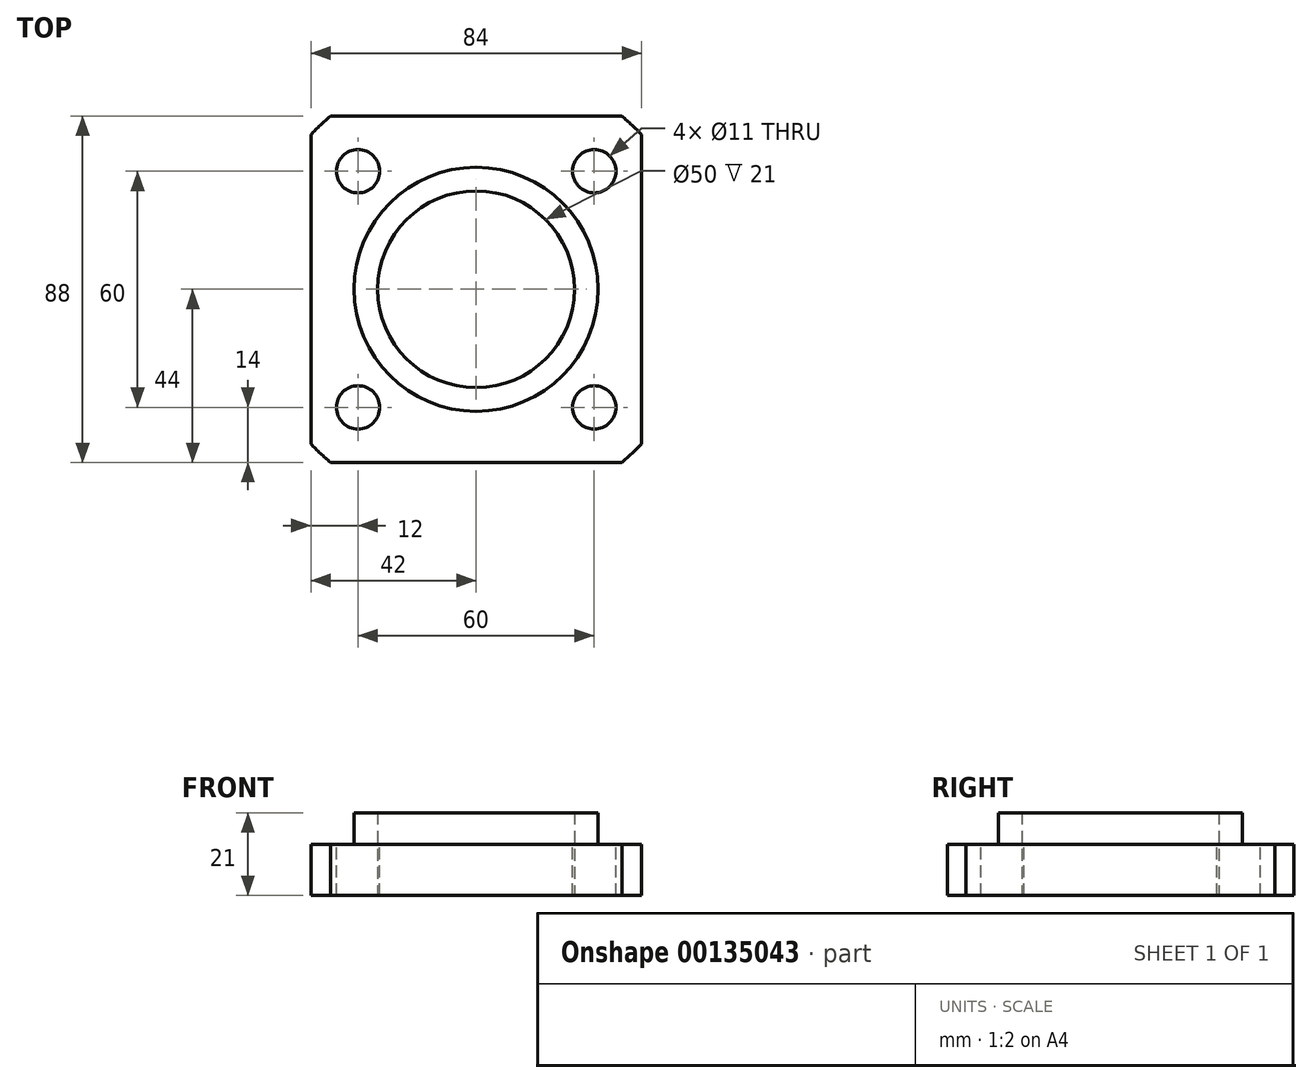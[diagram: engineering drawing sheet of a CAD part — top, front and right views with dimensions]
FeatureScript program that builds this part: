
annotation { "Feature Type Name" : "Feature", "Feature Type Description" : "" }
export const myFeature = defineFeature(function(context is Context, id is Id, definition is map)
    precondition{}
    {
        {
            var Q0;
            Q0=qCreatedBy(makeId("Top.planeOp"),FACE);
            var sketch = newSketch(context, id + "F0", { "sketchPlane" : qUnion([Q0])});
            skArc(sketch, "E0", {"start": v(-37.02, 44) * mm, "mid": v(-39.58, 41.71) * mm, "end": v(-42, 39.27) * mm});
            skLineSegment(sketch, "E1.bottom", {"start": v(37.02, -44) * mm, "end": v(-37.02, -44) * mm});
            skLineSegment(sketch, "E1.top", {"start": v(37.02, 44) * mm, "end": v(-37.02, 44) * mm});
            skLineSegment(sketch, "E1.left", {"start": v(42, -39.27) * mm, "end": v(42, 39.27) * mm});
            skLineSegment(sketch, "E1.right", {"start": v(-42, -39.27) * mm, "end": v(-42, 39.27) * mm});
            skArc(sketch, "E2.trimOffspring", {"start": v(-42, -39.27) * mm, "mid": v(-39.58, -41.71) * mm, "end": v(-37.02, -44) * mm});
            skArc(sketch, "E3.trimOffspring", {"start": v(42, 39.27) * mm, "mid": v(39.58, 41.71) * mm, "end": v(37.02, 44) * mm});
            skArc(sketch, "E4.trimOffspring", {"start": v(37.02, -44) * mm, "mid": v(39.58, -41.71) * mm, "end": v(42, -39.27) * mm});
            skPoint(sketch, "E5.orphan", {"position": v(-42, -44) * mm});
            skPoint(sketch, "E6.orphan", {"position": v(-42, 44) * mm});
            skPoint(sketch, "E7.orphan", {"position": v(42, -44) * mm});
            skPoint(sketch, "E8.orphan", {"position": v(42, 44) * mm});
            skSolve(sketch);
        }
        {
            var Q0;
            Q0 = qSketchRegion(id + "F0", true);
            extrude(context, id + "F1", {"entities" : qUnion([Q0]), "depth" : 13 * mm});
        }
        {
            var Q0;
            Q0=makeQuery(id+"F1.opExtrude","CAP_FACE",FACE,{"disambiguationData":[OSD([sQuery(id+"F0.wireOp",EDGE,"E0")])],"isStart":false});
            var sketch = newSketch(context, id + "F2", { "sketchPlane" : qUnion([Q0])});
            skCircle(sketch, "E9", {"center": v(0, 0) * mm, "radius": 31 * mm});
            skSolve(sketch);
        }
        {
            var Q0;
            Q0 = qSketchRegion(id + "F2", true);
            extrude(context, id + "F3", {"entities" : qUnion([Q0]), "operationType" : NewBodyOperationType.ADD, "depth" : 8 * mm});
        }
        {
            var Q0;
            Q0=sQuery(id+"F0.wireOp",VERTEX,"E0.center");
            var Q1;
            Q1=makeQuery(id+"F1.opExtrude","SWEPT_BODY",BODY,{"disambiguationData":[OSD([sQuery(id+"F0.wireOp",EDGE,"E0"),sQuery(id+"F0.wireOp",EDGE,"E1.bottom"),sQuery(id+"F0.wireOp",EDGE,"E1.top"),sQuery(id+"F0.wireOp",EDGE,"E1.left"),sQuery(id+"F0.wireOp",EDGE,"E1.right"),sQuery(id+"F0.wireOp",EDGE,"E2.trimOffspring"),sQuery(id+"F0.wireOp",EDGE,"E3.trimOffspring"),sQuery(id+"F0.wireOp",EDGE,"E4.trimOffspring")])]});
            hole(context, id + "F4", {"style" : HoleStyle.SIMPLE, "endStyle" : HoleEndStyle.THROUGH, "oppositeDirection" : true, "holeDiameter" : 50 * mm, "locations" : qUnion([Q0]), "scope" : qUnion([Q1]), "isTappedThrough" : true});
        }
        {
            var Q0;
            Q0=makeQuery(id+"F1.opExtrude","CAP_FACE",FACE,{"disambiguationData":[OSD([sQuery(id+"F0.wireOp",EDGE,"E0"),sQuery(id+"F0.wireOp",EDGE,"E1.bottom"),sQuery(id+"F0.wireOp",EDGE,"E1.top"),sQuery(id+"F0.wireOp",EDGE,"E1.left"),sQuery(id+"F0.wireOp",EDGE,"E1.right"),sQuery(id+"F0.wireOp",EDGE,"E2.trimOffspring"),sQuery(id+"F0.wireOp",EDGE,"E3.trimOffspring"),sQuery(id+"F0.wireOp",EDGE,"E4.trimOffspring")])],"isStart":false});
            var sketch = newSketch(context, id + "F5", { "sketchPlane" : qUnion([Q0])});
            skPoint(sketch, "E10", {"position": v(-30, 30) * mm});
            skPoint(sketch, "E11", {"position": v(-30, -30) * mm});
            skPoint(sketch, "E12", {"position": v(30, -30) * mm});
            skPoint(sketch, "E13", {"position": v(30, 30) * mm});
            skSolve(sketch);
        }
        {
            var Q0;
            Q0=sQuery(id+"F5.wireOp",VERTEX,"E10");
            var Q1;
            Q1=sQuery(id+"F5.wireOp",VERTEX,"E13");
            var Q2;
            Q2=sQuery(id+"F5.wireOp",VERTEX,"E11");
            var Q3;
            Q3=sQuery(id+"F5.wireOp",VERTEX,"E12");
            var Q4;
            Q4=makeQuery(id+"F1.opExtrude","SWEPT_BODY",BODY,{"disambiguationData":[OSD([sQuery(id+"F0.wireOp",EDGE,"E0"),sQuery(id+"F0.wireOp",EDGE,"E1.bottom"),sQuery(id+"F0.wireOp",EDGE,"E1.top"),sQuery(id+"F0.wireOp",EDGE,"E1.left"),sQuery(id+"F0.wireOp",EDGE,"E1.right"),sQuery(id+"F0.wireOp",EDGE,"E2.trimOffspring"),sQuery(id+"F0.wireOp",EDGE,"E3.trimOffspring"),sQuery(id+"F0.wireOp",EDGE,"E4.trimOffspring")])]});
            hole(context, id + "F6", {"style" : HoleStyle.SIMPLE, "endStyle" : HoleEndStyle.THROUGH, "holeDiameter" : 11 * mm, "locations" : qUnion([Q0, Q1, Q2, Q3]), "scope" : qUnion([Q4]), "isTappedThrough" : true});
        }
    });
